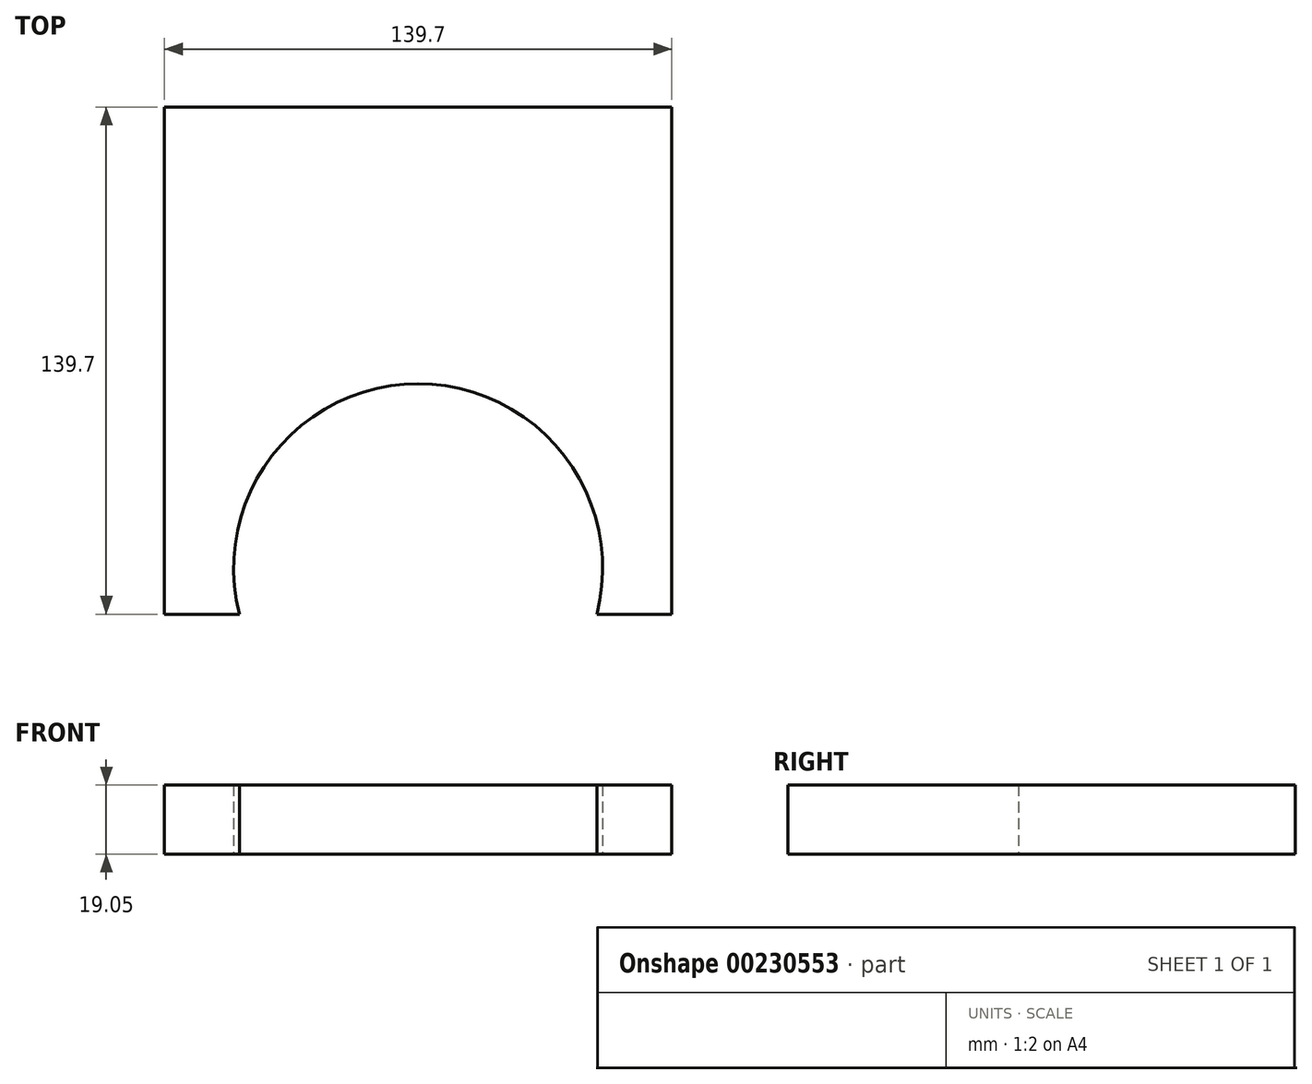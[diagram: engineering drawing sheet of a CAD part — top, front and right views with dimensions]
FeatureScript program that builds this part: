
annotation { "Feature Type Name" : "Feature", "Feature Type Description" : "" }
export const myFeature = defineFeature(function(context is Context, id is Id, definition is map)
    precondition{}
    {
        {
            var Q0;
            Q0=qCreatedBy(makeId("Top.planeOp"),FACE);
            var sketch = newSketch(context, id + "F0", { "sketchPlane" : qUnion([Q0])});
            skLineSegment(sketch, "E0.bottom", {"start": v(-69.85, 69.82) * mm, "end": v(69.85, 69.82) * mm});
            skLineSegment(sketch, "E0.top", {"start": v(-69.85, -69.88) * mm, "end": v(-49.19, -69.88) * mm});
            skLineSegment(sketch, "E0.left", {"start": v(-69.85, 69.82) * mm, "end": v(-69.85, -69.88) * mm});
            skLineSegment(sketch, "E0.right", {"start": v(69.85, 69.82) * mm, "end": v(69.85, -69.88) * mm});
            skPoint(sketch, "E0.middle", {"position": v(0, -0.03) * mm});
            skLineSegment(sketch, "E1", {"start": v(0, -69.88) * mm, "end": v(0, -57.18) * mm});
            skPoint(sketch, "E1.endSnap0", {"position": v(0, -69.88) * mm});
            skArc(sketch, "E2", {"start": v(49.19, -69.88) * mm, "mid": v(0, -6.38) * mm, "end": v(-49.19, -69.88) * mm});
            skLineSegment(sketch, "E3.trimOffspring", {"start": v(49.19, -69.88) * mm, "end": v(69.85, -69.88) * mm});
            skSolve(sketch);
        }
        {
            var Q0;
            Q0=makeQuery(id+"F0.imprint","IMPRINT",FACE,{"disambiguationData":[TD([[makeQuery(id+"F0.imprint","IMPRINT",EDGE,{"derivedFrom":sQuery(id+"F0.wireOp",EDGE,"E0.bottom")}),-1.0]])]});
            extrude(context, id + "F1", {"entities" : qUnion([Q0]), "depth" : 19.05 * mm});
        }
    });
